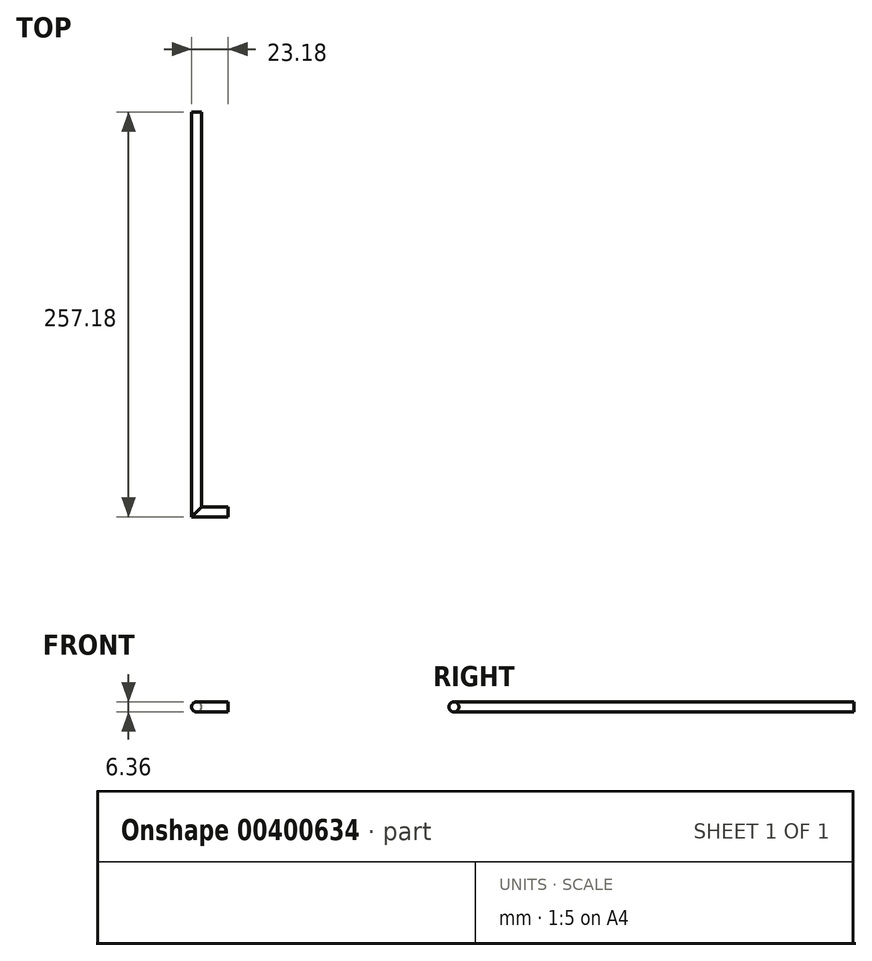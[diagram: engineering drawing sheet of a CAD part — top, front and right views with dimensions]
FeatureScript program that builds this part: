
annotation { "Feature Type Name" : "Feature", "Feature Type Description" : "" }
export const myFeature = defineFeature(function(context is Context, id is Id, definition is map)
    precondition{}
    {
        {
            var Q0;
            Q0=qCreatedBy(makeId("Front.planeOp"),FACE);
            var sketch = newSketch(context, id + "F0", { "sketchPlane" : qUnion([Q0])});
            skCircle(sketch, "E0", {"center": v(0, 0) * mm, "radius": 3.18 * mm});
            skSolve(sketch);
        }
        {
            var Q0;
            Q0=qCreatedBy(makeId("Top.planeOp"),FACE);
            var sketch = newSketch(context, id + "F1", { "sketchPlane" : qUnion([Q0])});
            skLineSegment(sketch, "E1", {"start": v(0, 0) * mm, "end": v(0, -254) * mm});
            skLineSegment(sketch, "E2", {"start": v(0, -254) * mm, "end": v(20, -254) * mm});
            skSolve(sketch);
        }
        {
            var Q0;
            Q0=makeQuery(id+"F0.imprint","IMPRINT",FACE,{"disambiguationData":[TD([[makeQuery(id+"F0.imprint","IMPRINT",EDGE,{"derivedFrom":sQuery(id+"F0.wireOp",EDGE,"E0")}),1.0]])]});
            var Q1;
            Q1=sQuery(id+"F1.wireOp",EDGE,"E1");
            var Q2;
            Q2=sQuery(id+"F1.wireOp",EDGE,"E1");
            var Q3;
            Q3=sQuery(id+"F1.wireOp",EDGE,"E2");
            sweep(context, id + "F2", {"profiles" : qUnion([Q0]), "path" : qUnion([Q1, Q2, Q3])});
        }
    });
